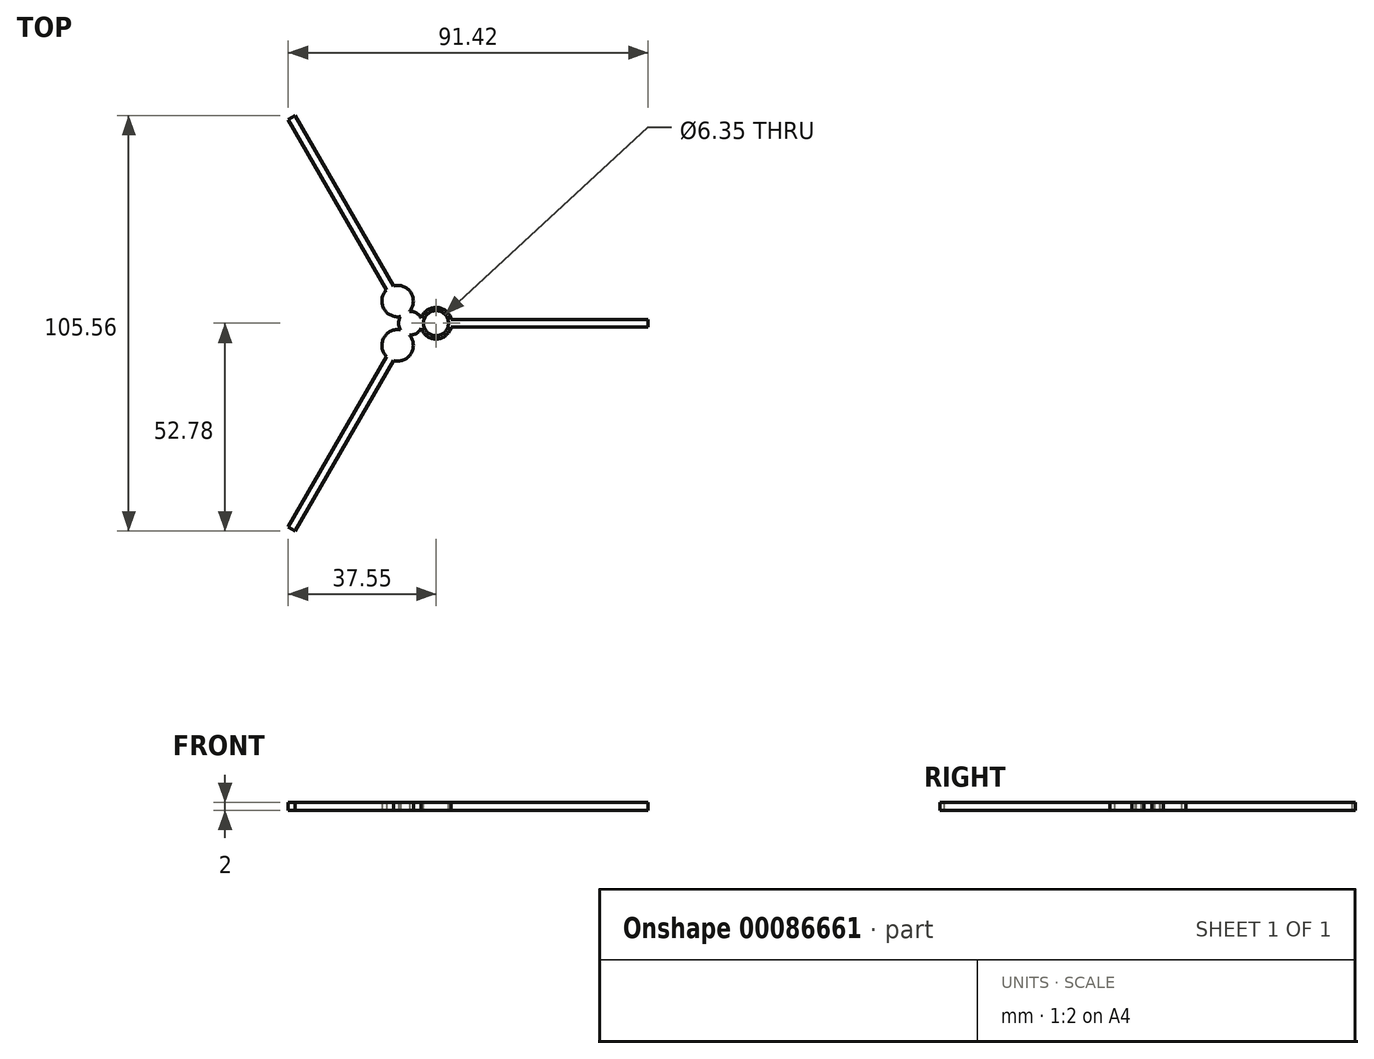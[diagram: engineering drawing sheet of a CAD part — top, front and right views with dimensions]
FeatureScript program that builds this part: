
annotation { "Feature Type Name" : "Feature", "Feature Type Description" : "" }
export const myFeature = defineFeature(function(context is Context, id is Id, definition is map)
    precondition{}
    {
        {
            var Q0;
            Q0=qCreatedBy(makeId("Top.planeOp"),FACE);
            var sketch = newSketch(context, id + "F0", { "sketchPlane" : qUnion([Q0])});
            skCircle(sketch, "E0", {"center": v(0, 0) * mm, "radius": 3 * mm});
            skCircle(sketch, "E1", {"center": v(6.5, 0) * mm, "radius": 4 * mm});
            skCircle(sketch, "E2.1.0", {"center": v(-3.25, 5.63) * mm, "radius": 4 * mm});
            skCircle(sketch, "E2.2.0", {"center": v(-3.25, -5.63) * mm, "radius": 4 * mm});
            skLineSegment(sketch, "E3.bottom", {"start": v(10.37, -1) * mm, "end": v(60.37, -1) * mm});
            skLineSegment(sketch, "E3.top", {"start": v(10.37, 1) * mm, "end": v(60.37, 1) * mm});
            skLineSegment(sketch, "E3.left", {"start": v(10.37, -1) * mm, "end": v(10.37, 1) * mm});
            skLineSegment(sketch, "E3.right", {"start": v(60.37, -1) * mm, "end": v(60.37, 1) * mm});
            skLineSegment(sketch, "E4.1.0", {"start": v(-6.05, 8.48) * mm, "end": v(-31.05, 51.78) * mm});
            skLineSegment(sketch, "E4.1.1", {"start": v(-4.32, 9.48) * mm, "end": v(-29.32, 52.78) * mm});
            skLineSegment(sketch, "E4.1.2", {"start": v(-29.32, 52.78) * mm, "end": v(-31.05, 51.78) * mm});
            skLineSegment(sketch, "E4.1.3", {"start": v(-4.32, 9.48) * mm, "end": v(-6.05, 8.48) * mm});
            skLineSegment(sketch, "E4.2.0", {"start": v(-4.32, -9.48) * mm, "end": v(-29.32, -52.78) * mm});
            skLineSegment(sketch, "E4.2.1", {"start": v(-6.05, -8.48) * mm, "end": v(-31.05, -51.78) * mm});
            skLineSegment(sketch, "E4.2.2", {"start": v(-31.05, -51.78) * mm, "end": v(-29.32, -52.78) * mm});
            skLineSegment(sketch, "E4.2.3", {"start": v(-6.05, -8.48) * mm, "end": v(-4.32, -9.48) * mm});
            skSolve(sketch);
        }
        {
            var Q0;
            {var subQ0=sQuery(id+"F0.wireOp",EDGE,"E1");var subQ1=sQuery(id+"F0.wireOp",EDGE,"E0");var subQ2=makeQuery(id+"F0.imprint","INTERSECT",VERTEX,{"disambiguationData":[OD(0.0)],"derivedFrom":[subQ1,subQ0]});Q0=makeQuery(id+"F0.imprint","IMPRINT",FACE,{"disambiguationData":[TD([[makeQuery(id+"F0.imprint","IMPRINT",EDGE,{"disambiguationData":[TD([[subQ2,1.0]])],"derivedFrom":subQ1}),1.0]])]});}
            var Q1;
            {var subQ0=sQuery(id+"F0.wireOp",EDGE,"E1");var subQ1=sQuery(id+"F0.wireOp",EDGE,"E0");var subQ2=makeQuery(id+"F0.imprint","INTERSECT",VERTEX,{"disambiguationData":[OD(0.0)],"derivedFrom":[subQ1,subQ0]});Q1=makeQuery(id+"F0.imprint","IMPRINT",FACE,{"disambiguationData":[TD([[makeQuery(id+"F0.imprint","IMPRINT",EDGE,{"disambiguationData":[TD([[subQ2,-1.0]])],"derivedFrom":subQ1}),1.0]])]});}
            var Q2;
            {var subQ0=sQuery(id+"F0.wireOp",EDGE,"E1");var subQ1=sQuery(id+"F0.wireOp",EDGE,"E0");var subQ2=makeQuery(id+"F0.imprint","INTERSECT",VERTEX,{"disambiguationData":[OD(0.0)],"derivedFrom":[subQ1,subQ0]});Q2=makeQuery(id+"F0.imprint","IMPRINT",FACE,{"disambiguationData":[TD([[makeQuery(id+"F0.imprint","IMPRINT",EDGE,{"disambiguationData":[TD([[subQ2,-1.0]])],"derivedFrom":subQ1}),-1.0]])]});}
            var Q3;
            {var subQ0=sQuery(id+"F0.wireOp",EDGE,"E2.1.0");var subQ1=sQuery(id+"F0.wireOp",EDGE,"E0");var subQ2=makeQuery(id+"F0.imprint","INTERSECT",VERTEX,{"disambiguationData":[OD(0.0)],"derivedFrom":[subQ1,subQ0]});Q3=makeQuery(id+"F0.imprint","IMPRINT",FACE,{"disambiguationData":[TD([[makeQuery(id+"F0.imprint","IMPRINT",EDGE,{"disambiguationData":[TD([[subQ2,-1.0]])],"derivedFrom":subQ1}),-1.0]])]});}
            var Q4;
            {var subQ0=sQuery(id+"F0.wireOp",EDGE,"E2.1.0");var subQ1=sQuery(id+"F0.wireOp",EDGE,"E0");var subQ2=makeQuery(id+"F0.imprint","INTERSECT",VERTEX,{"disambiguationData":[OD(0.0)],"derivedFrom":[subQ1,subQ0]});Q4=makeQuery(id+"F0.imprint","IMPRINT",FACE,{"disambiguationData":[TD([[makeQuery(id+"F0.imprint","IMPRINT",EDGE,{"disambiguationData":[TD([[subQ2,-1.0]])],"derivedFrom":subQ1}),1.0]])]});}
            var Q5;
            {var subQ0=sQuery(id+"F0.wireOp",EDGE,"E2.2.0");var subQ1=sQuery(id+"F0.wireOp",EDGE,"E0");var subQ2=makeQuery(id+"F0.imprint","INTERSECT",VERTEX,{"disambiguationData":[OD(0.0)],"derivedFrom":[subQ1,subQ0]});Q5=makeQuery(id+"F0.imprint","IMPRINT",FACE,{"disambiguationData":[TD([[makeQuery(id+"F0.imprint","IMPRINT",EDGE,{"disambiguationData":[TD([[subQ2,-1.0]])],"derivedFrom":subQ1}),1.0]])]});}
            var Q6;
            {var subQ0=sQuery(id+"F0.wireOp",EDGE,"E2.2.0");var subQ1=sQuery(id+"F0.wireOp",EDGE,"E0");var subQ2=makeQuery(id+"F0.imprint","INTERSECT",VERTEX,{"disambiguationData":[OD(0.0)],"derivedFrom":[subQ1,subQ0]});Q6=makeQuery(id+"F0.imprint","IMPRINT",FACE,{"disambiguationData":[TD([[makeQuery(id+"F0.imprint","IMPRINT",EDGE,{"disambiguationData":[TD([[subQ2,-1.0]])],"derivedFrom":subQ1}),-1.0]])]});}
            var Q7;
            {var subQ0=sQuery(id+"F0.wireOp",EDGE,"E1");var subQ1=sQuery(id+"F0.wireOp",EDGE,"E0");var subQ2=makeQuery(id+"F0.imprint","INTERSECT",VERTEX,{"disambiguationData":[OD(0.0)],"derivedFrom":[subQ1,subQ0]});Q7=makeQuery(id+"F0.imprint","IMPRINT",FACE,{"disambiguationData":[TD([[makeQuery(id+"F0.imprint","IMPRINT",EDGE,{"disambiguationData":[TD([[subQ2,1.0]])],"derivedFrom":subQ1}),-1.0]])]});}
            var Q8;
            {var subQ1=sQuery(id+"F0.wireOp",EDGE,"E3.bottom");Q8=makeQuery(id+"F0.imprint","IMPRINT",FACE,{"disambiguationData":[TD([[makeQuery(id+"F0.imprint","IMPRINT",EDGE,{"derivedFrom":subQ1}),1.0]])]});}
            var Q9;
            {var subQ0=sQuery(id+"F0.wireOp",EDGE,"E3.left");Q9=makeQuery(id+"F0.imprint","IMPRINT",FACE,{"disambiguationData":[TD([[makeQuery(id+"F0.imprint","IMPRINT",EDGE,{"derivedFrom":subQ0}),-1.0]])]});}
            var Q10;
            {var subQ0=sQuery(id+"F0.wireOp",EDGE,"E4.2.3");Q10=makeQuery(id+"F0.imprint","IMPRINT",FACE,{"disambiguationData":[TD([[makeQuery(id+"F0.imprint","IMPRINT",EDGE,{"derivedFrom":subQ0}),-1.0]])]});}
            var Q11;
            {var subQ1=sQuery(id+"F0.wireOp",EDGE,"E4.2.0");Q11=makeQuery(id+"F0.imprint","IMPRINT",FACE,{"disambiguationData":[TD([[makeQuery(id+"F0.imprint","IMPRINT",EDGE,{"derivedFrom":subQ1}),-1.0]])]});}
            var Q12;
            {var subQ0=sQuery(id+"F0.wireOp",EDGE,"E4.1.3");Q12=makeQuery(id+"F0.imprint","IMPRINT",FACE,{"disambiguationData":[TD([[makeQuery(id+"F0.imprint","IMPRINT",EDGE,{"derivedFrom":subQ0}),-1.0]])]});}
            var Q13;
            {var subQ1=sQuery(id+"F0.wireOp",EDGE,"E4.1.0");Q13=makeQuery(id+"F0.imprint","IMPRINT",FACE,{"disambiguationData":[TD([[makeQuery(id+"F0.imprint","IMPRINT",EDGE,{"derivedFrom":subQ1}),-1.0]])]});}
            extrude(context, id + "F1", {"entities" : qUnion([Q0, Q1, Q2, Q3, Q4, Q5, Q6, Q7, Q8, Q9, Q10, Q11, Q12, Q13]), "depth" : 2 * mm});
        }
        {
            var Q0;
            Q0=makeQuery(id+"F1.opExtrude","CAP_FACE",FACE,{"disambiguationData":[OSD([sQuery(id+"F0.wireOp",EDGE,"E0"),sQuery(id+"F0.wireOp",EDGE,"E1"),sQuery(id+"F0.wireOp",EDGE,"E2.1.0"),sQuery(id+"F0.wireOp",EDGE,"E2.2.0"),sQuery(id+"F0.wireOp",EDGE,"E3.bottom"),sQuery(id+"F0.wireOp",EDGE,"E3.top"),sQuery(id+"F0.wireOp",EDGE,"E3.right"),sQuery(id+"F0.wireOp",EDGE,"E4.1.0"),sQuery(id+"F0.wireOp",EDGE,"E4.1.1"),sQuery(id+"F0.wireOp",EDGE,"E4.1.2"),sQuery(id+"F0.wireOp",EDGE,"E4.2.0"),sQuery(id+"F0.wireOp",EDGE,"E4.2.1"),sQuery(id+"F0.wireOp",EDGE,"E4.2.2")])],"isStart":false});
            var sketch = newSketch(context, id + "F2", { "sketchPlane" : qUnion([Q0])});
            skCircle(sketch, "E5", {"center": v(6.5, 0) * mm, "radius": 3.17 * mm});
            skSolve(sketch);
        }
        {
            var Q0;
            Q0 = qSketchRegion(id + "F2", true);
            extrude(context, id + "F3", {"entities" : qUnion([Q0]), "operationType" : NewBodyOperationType.REMOVE, "oppositeDirection" : true, "depth" : 25 * mm});
        }
    });
